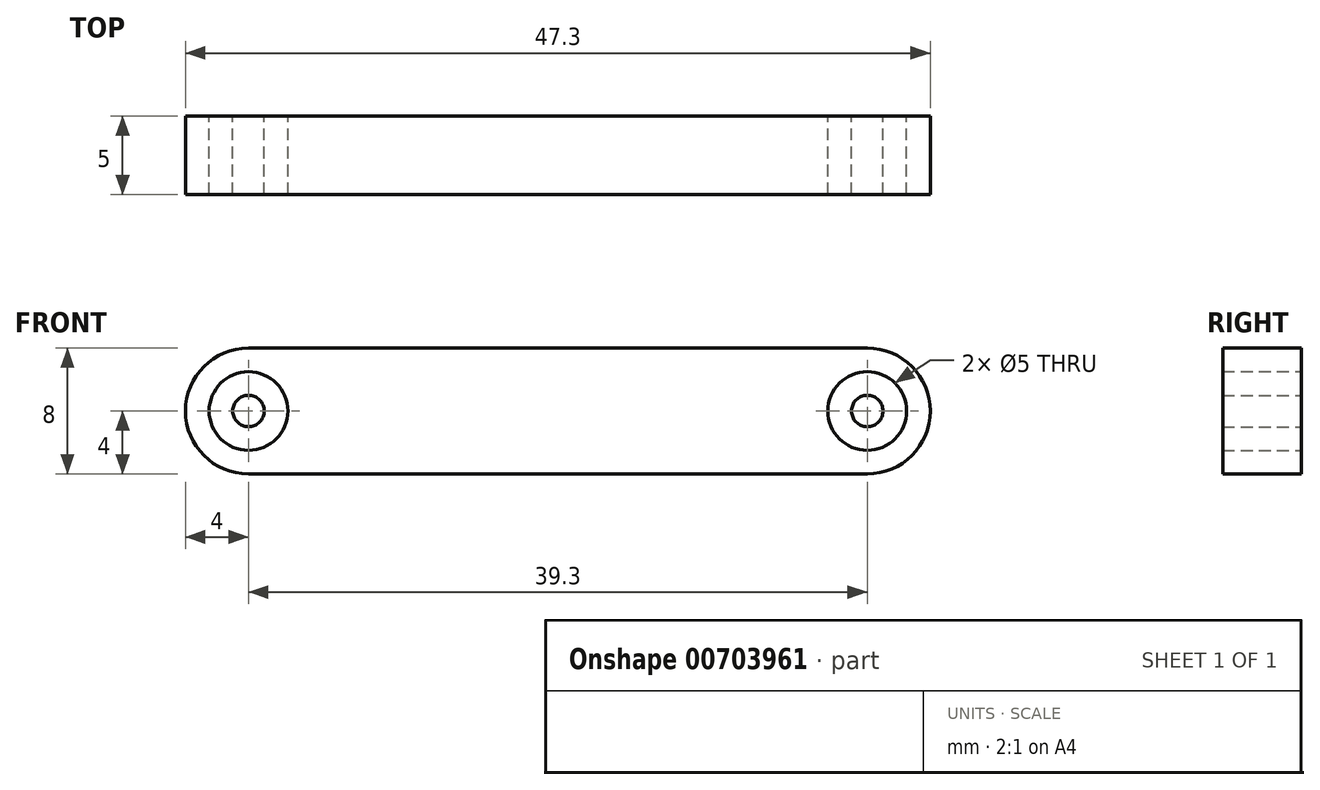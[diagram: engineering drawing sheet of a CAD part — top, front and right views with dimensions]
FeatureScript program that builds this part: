
annotation { "Feature Type Name" : "Feature", "Feature Type Description" : "" }
export const myFeature = defineFeature(function(context is Context, id is Id, definition is map)
    precondition{}
    {
        {
            var Q0;
            Q0=qCreatedBy(makeId("Front.planeOp"),FACE);
            var sketch = newSketch(context, id + "F0", { "sketchPlane" : qUnion([Q0])});
            skCircle(sketch, "E0", {"center": v(0, 0) * mm, "radius": 2.5 * mm});
            skArc(sketch, "E1", {"start": v(0, -4) * mm, "mid": v(-4, 0) * mm, "end": v(0, 4) * mm});
            skCircle(sketch, "E2", {"center": v(39.3, 0) * mm, "radius": 2.5 * mm});
            skArc(sketch, "E3", {"start": v(39.3, -4) * mm, "mid": v(43.3, 0) * mm, "end": v(39.3, 4) * mm});
            skLineSegment(sketch, "E4", {"start": v(0, 4) * mm, "end": v(39.3, 4) * mm});
            skLineSegment(sketch, "E5", {"start": v(0, -4) * mm, "end": v(39.3, -4) * mm});
            skCircle(sketch, "E6", {"center": v(0, 0) * mm, "radius": 1 * mm});
            skCircle(sketch, "E7", {"center": v(39.3, 0) * mm, "radius": 1 * mm});
            skSolve(sketch);
        }
        {
            var Q0;
            Q0=makeQuery(id+"F0.imprint","IMPRINT",FACE,{"disambiguationData":[TD([[makeQuery(id+"F0.imprint","IMPRINT",EDGE,{"derivedFrom":sQuery(id+"F0.wireOp",EDGE,"E0")}),-1.0]])]});
            var Q1;
            Q1=makeQuery(id+"F0.imprint","IMPRINT",FACE,{"disambiguationData":[TD([[makeQuery(id+"F0.imprint","IMPRINT",EDGE,{"derivedFrom":sQuery(id+"F0.wireOp",EDGE,"E6")}),1.0]])]});
            var Q2;
            Q2=makeQuery(id+"F0.imprint","IMPRINT",FACE,{"disambiguationData":[TD([[makeQuery(id+"F0.imprint","IMPRINT",EDGE,{"derivedFrom":sQuery(id+"F0.wireOp",EDGE,"E7")}),1.0]])]});
            extrude(context, id + "F1", {"entities" : qUnion([Q0, Q1, Q2]), "depth" : 5 * mm, "offsetDistance" : 25 * mm});
        }
    });
